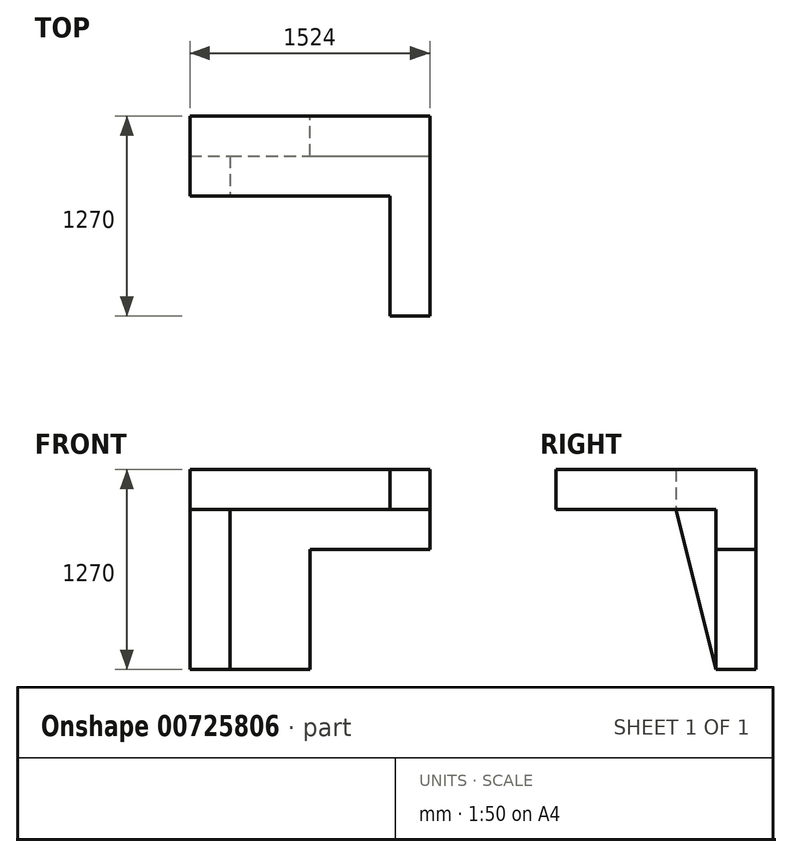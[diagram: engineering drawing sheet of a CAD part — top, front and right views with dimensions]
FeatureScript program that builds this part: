
annotation { "Feature Type Name" : "Feature", "Feature Type Description" : "" }
export const myFeature = defineFeature(function(context is Context, id is Id, definition is map)
    precondition{}
    {
        {
            var Q0;
            Q0=qCreatedBy(makeId("Front.planeOp"),FACE);
            var sketch = newSketch(context, id + "F0", { "sketchPlane" : qUnion([Q0])});
            skLineSegment(sketch, "E0", {"start": v(0, 0) * mm, "end": v(762, 0) * mm});
            skLineSegment(sketch, "E1", {"start": v(762, 0) * mm, "end": v(762, 762) * mm});
            skLineSegment(sketch, "E2", {"start": v(762, 762) * mm, "end": v(1524, 762) * mm});
            skLineSegment(sketch, "E3", {"start": v(1524, 762) * mm, "end": v(1524, 1270) * mm});
            skLineSegment(sketch, "E4", {"start": v(1524, 1270) * mm, "end": v(0, 1270) * mm});
            skLineSegment(sketch, "E5", {"start": v(0, 1270) * mm, "end": v(0, 0) * mm});
            skSolve(sketch);
        }
        {
            var Q0;
            Q0 = qSketchRegion(id + "F0", true);
            extrude(context, id + "F1", {"entities" : qUnion([Q0]), "depth" : 1270 * mm, "offsetDistance" : 25.4 * mm});
        }
        {
            var Q0;
            Q0=makeQuery(id+"F1.opExtrude","CAP_FACE",FACE,{"disambiguationData":[OSD([sQuery(id+"F0.wireOp",EDGE,"E0"),sQuery(id+"F0.wireOp",EDGE,"E1"),sQuery(id+"F0.wireOp",EDGE,"E2"),sQuery(id+"F0.wireOp",EDGE,"E3"),sQuery(id+"F0.wireOp",EDGE,"E4"),sQuery(id+"F0.wireOp",EDGE,"E5")])],"isStart":false});
            var sketch = newSketch(context, id + "F2", { "sketchPlane" : qUnion([Q0])});
            skLineSegment(sketch, "E6", {"start": v(762, 762) * mm, "end": v(254, 762) * mm});
            skLineSegment(sketch, "E7", {"start": v(254, 762) * mm, "end": v(254, 0) * mm});
            skLineSegment(sketch, "E8", {"start": v(254, 0) * mm, "end": v(762, 0) * mm});
            skLineSegment(sketch, "E9", {"start": v(762, 0) * mm, "end": v(762, 762) * mm});
            skSolve(sketch);
        }
        {
            var Q0;
            Q0 = qSketchRegion(id + "F2", true);
            extrude(context, id + "F3", {"entities" : qUnion([Q0]), "operationType" : NewBodyOperationType.REMOVE, "oppositeDirection" : true, "depth" : 1016 * mm, "offsetDistance" : 25.4 * mm});
        }
        {
            var Q0;
            Q0=makeQuery(id+"F1.opExtrude","CAP_FACE",FACE,{"disambiguationData":[OSD([sQuery(id+"F0.wireOp",EDGE,"E0"),sQuery(id+"F0.wireOp",EDGE,"E1"),sQuery(id+"F0.wireOp",EDGE,"E2"),sQuery(id+"F0.wireOp",EDGE,"E3"),sQuery(id+"F0.wireOp",EDGE,"E4"),sQuery(id+"F0.wireOp",EDGE,"E5")])],"isStart":false});
            var sketch = newSketch(context, id + "F4", { "sketchPlane" : qUnion([Q0])});
            skLineSegment(sketch, "E10", {"start": v(254, 762) * mm, "end": v(254, 1016) * mm});
            skLineSegment(sketch, "E11", {"start": v(254, 1016) * mm, "end": v(1524, 1016) * mm});
            skLineSegment(sketch, "E12", {"start": v(1524, 1016) * mm, "end": v(1524, 762) * mm});
            skLineSegment(sketch, "E13", {"start": v(1524, 762) * mm, "end": v(254, 762) * mm});
            skSolve(sketch);
        }
        {
            var Q0;
            Q0 = qSketchRegion(id + "F4", true);
            extrude(context, id + "F5", {"entities" : qUnion([Q0]), "operationType" : NewBodyOperationType.REMOVE, "oppositeDirection" : true, "depth" : 1016 * mm, "offsetDistance" : 25.4 * mm});
        }
        {
            var Q0;
            Q0=makeQuery(id+"F5.boolean.opBoolean","MERGE",FACE,{"derivedFrom":[makeQuery(id+"F3.boolean.opBoolean","COPY",FACE,{"derivedFrom":makeQuery(id+"F3.opExtrude","SWEPT_FACE",FACE,{"disambiguationData":[OSD([sQuery(id+"F2.wireOp",EDGE,"E7")])]})}),makeQuery(id+"F5.opExtrude","SWEPT_FACE",FACE,{"disambiguationData":[OSD([sQuery(id+"F4.wireOp",EDGE,"E10")])]})]});
            var sketch = newSketch(context, id + "F6", { "sketchPlane" : qUnion([Q0])});
            skLineSegment(sketch, "E14", {"start": v(-1270, 1016) * mm, "end": v(-254, 0) * mm});
            skLineSegment(sketch, "E15", {"start": v(-254, 0) * mm, "end": v(-1270, 0) * mm});
            skLineSegment(sketch, "E16", {"start": v(-1270, 0) * mm, "end": v(-1270, 1016) * mm});
            skSolve(sketch);
        }
        {
            var Q0;
            Q0 = qSketchRegion(id + "F6", true);
            extrude(context, id + "F7", {"entities" : qUnion([Q0]), "operationType" : NewBodyOperationType.REMOVE, "endBound" : BoundingType.THROUGH_ALL, "oppositeDirection" : true, "depth" : 25.4 * mm, "offsetDistance" : 25.4 * mm});
        }
        {
            var Q0;
            Q0=makeQuery(id+"F5.boolean.opBoolean","COPY",FACE,{"derivedFrom":makeQuery(id+"F5.opExtrude","SWEPT_FACE",FACE,{"disambiguationData":[OSD([sQuery(id+"F4.wireOp",EDGE,"E11")])]})});
            var sketch = newSketch(context, id + "F8", { "sketchPlane" : qUnion([Q0])});
            skLineSegment(sketch, "E17", {"start": v(508, 1270) * mm, "end": v(508, 508) * mm});
            skLineSegment(sketch, "E18", {"start": v(508, 508) * mm, "end": v(1270, 508) * mm});
            skLineSegment(sketch, "E19", {"start": v(1270, 508) * mm, "end": v(1270, 1270) * mm});
            skLineSegment(sketch, "E20", {"start": v(1270, 1270) * mm, "end": v(508, 1270) * mm});
            skSolve(sketch);
        }
        {
            var Q0;
            Q0 = qSketchRegion(id + "F8", true);
            extrude(context, id + "F9", {"entities" : qUnion([Q0]), "operationType" : NewBodyOperationType.REMOVE, "endBound" : BoundingType.THROUGH_ALL, "oppositeDirection" : true, "depth" : 25.4 * mm, "offsetDistance" : 25.4 * mm});
        }
        {
            var Q0;
            {var subQ0=sQuery(id+"F0.wireOp",EDGE,"E4");var subQ1=sQuery(id+"F0.wireOp",EDGE,"E5");Q0=makeQuery(id+"F9.boolean.opBoolean","SPLIT",FACE,{"disambiguationData":[TD([makeQuery(id+"F1.opExtrude","SWEPT_FACE",FACE,{"disambiguationData":[OSD([subQ1])]})])],"derivedFrom":makeQuery(id+"F1.opExtrude","CAP_FACE",FACE,{"disambiguationData":[OSD([sQuery(id+"F0.wireOp",EDGE,"E0"),sQuery(id+"F0.wireOp",EDGE,"E1"),sQuery(id+"F0.wireOp",EDGE,"E2"),sQuery(id+"F0.wireOp",EDGE,"E3"),subQ0,subQ1])],"isStart":false})});}
            var sketch = newSketch(context, id + "F10", { "sketchPlane" : qUnion([Q0])});
            skLineSegment(sketch, "E21", {"start": v(0, 1270) * mm, "end": v(508, 1270) * mm});
            skLineSegment(sketch, "E22", {"start": v(508, 1270) * mm, "end": v(508, 1016) * mm});
            skLineSegment(sketch, "E23", {"start": v(508, 1016) * mm, "end": v(0, 1016) * mm});
            skLineSegment(sketch, "E24", {"start": v(0, 1016) * mm, "end": v(0, 1270) * mm});
            skSolve(sketch);
        }
        {
            var Q0;
            Q0 = qSketchRegion(id + "F10", true);
            extrude(context, id + "F11", {"entities" : qUnion([Q0]), "operationType" : NewBodyOperationType.REMOVE, "oppositeDirection" : true, "depth" : 762 * mm, "offsetDistance" : 25.4 * mm});
        }
        {
            var Q0;
            Q0=makeQuery(id+"F11.boolean.opBoolean","COPY",FACE,{"derivedFrom":makeQuery(id+"F11.opExtrude","SWEPT_FACE",FACE,{"disambiguationData":[OSD([sQuery(id+"F10.wireOp",EDGE,"E23")])]})});
            var sketch = newSketch(context, id + "F12", { "sketchPlane" : qUnion([Q0])});
            skLineSegment(sketch, "E25", {"start": v(254, -1270) * mm, "end": v(0, -1270) * mm});
            skLineSegment(sketch, "E26", {"start": v(0, -1270) * mm, "end": v(0, -508) * mm});
            skLineSegment(sketch, "E27", {"start": v(0, -508) * mm, "end": v(254, -508) * mm});
            skLineSegment(sketch, "E28", {"start": v(254, -508) * mm, "end": v(254, -1270) * mm});
            skSolve(sketch);
        }
        {
            var Q0;
            Q0 = qSketchRegion(id + "F12", true);
            extrude(context, id + "F13", {"entities" : qUnion([Q0]), "operationType" : NewBodyOperationType.REMOVE, "endBound" : BoundingType.THROUGH_ALL, "oppositeDirection" : true, "depth" : 25.4 * mm, "offsetDistance" : 25.4 * mm});
        }
        {
            var Q0;
            Q0=makeQuery(id+"F5.boolean.opBoolean","MERGE",FACE,{"derivedFrom":[makeQuery(id+"F3.boolean.opBoolean","COPY",FACE,{"derivedFrom":makeQuery(id+"F3.opExtrude","SWEPT_FACE",FACE,{"disambiguationData":[OSD([sQuery(id+"F2.wireOp",EDGE,"E7")])]})}),makeQuery(id+"F5.opExtrude","SWEPT_FACE",FACE,{"disambiguationData":[OSD([sQuery(id+"F4.wireOp",EDGE,"E10")])]})]});
            var sketch = newSketch(context, id + "F14", { "sketchPlane" : qUnion([Q0])});
            skLineSegment(sketch, "E29", {"start": v(-508, 1016) * mm, "end": v(-254, 0) * mm});
            skLineSegment(sketch, "E30", {"start": v(-254, 0) * mm, "end": v(-508, 254) * mm});
            skLineSegment(sketch, "E31", {"start": v(-508, 254) * mm, "end": v(-508, 1016) * mm});
            skSolve(sketch);
        }
        {
            var Q0;
            Q0 = qSketchRegion(id + "F14", true);
            extrude(context, id + "F15", {"entities" : qUnion([Q0]), "operationType" : NewBodyOperationType.REMOVE, "endBound" : BoundingType.THROUGH_ALL, "oppositeDirection" : true, "depth" : 25.4 * mm, "offsetDistance" : 25.4 * mm});
        }
    });
